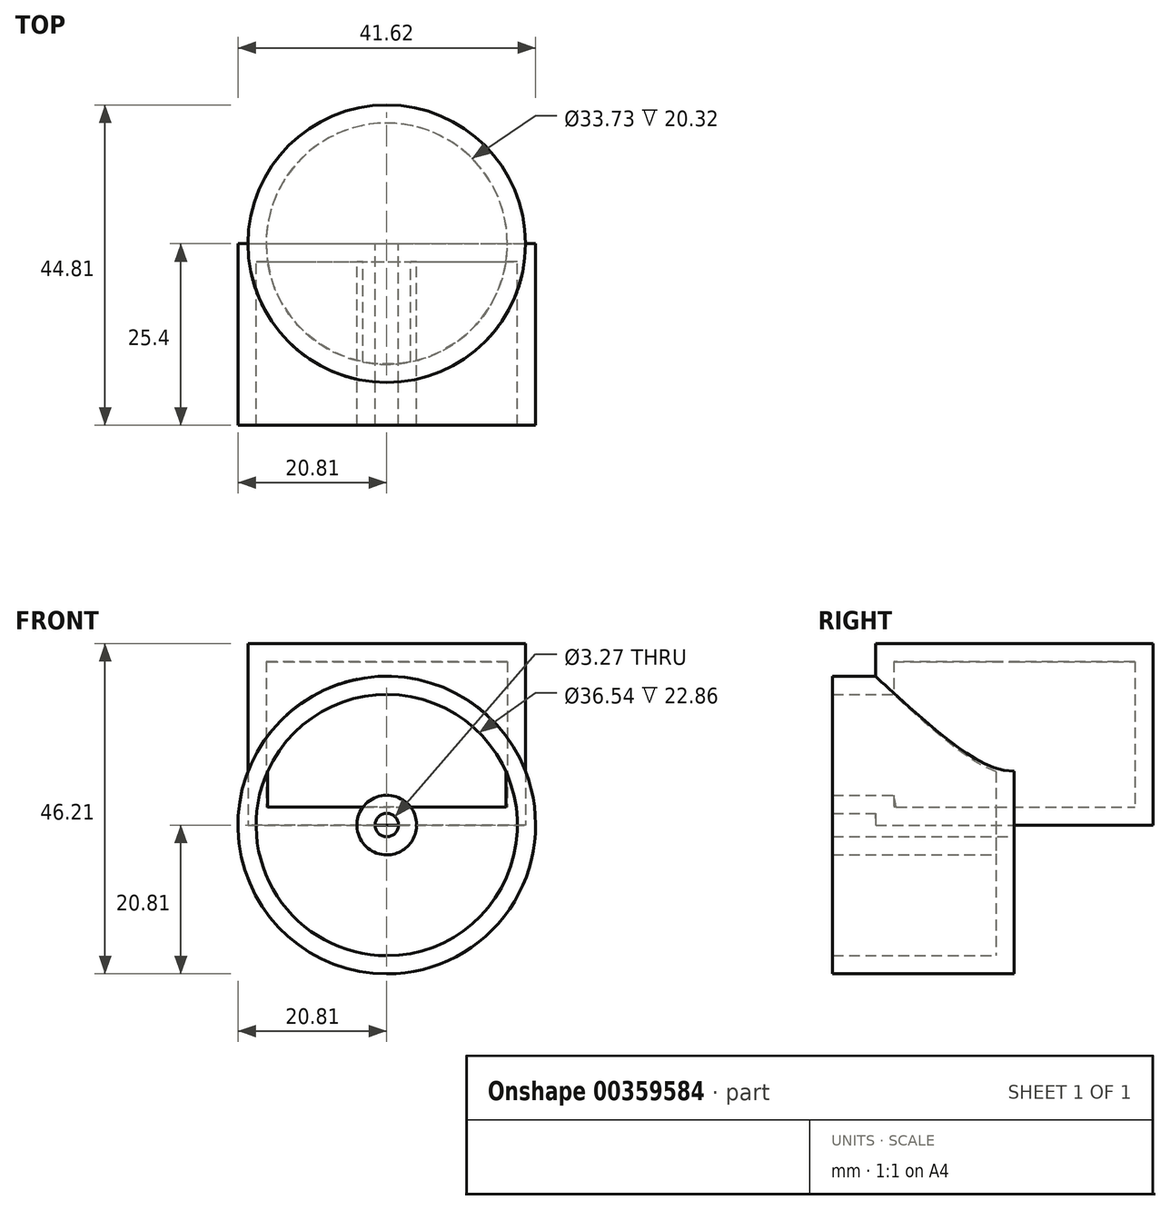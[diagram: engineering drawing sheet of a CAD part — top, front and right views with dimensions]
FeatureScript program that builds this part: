
annotation { "Feature Type Name" : "Feature", "Feature Type Description" : "" }
export const myFeature = defineFeature(function(context is Context, id is Id, definition is map)
    precondition{}
    {
        {
            var Q0;
            Q0=qCreatedBy(makeId("Top.planeOp"),FACE);
            var sketch = newSketch(context, id + "F0", { "sketchPlane" : qUnion([Q0])});
            skCircle(sketch, "E0", {"center": v(0, 0) * mm, "radius": 19.4 * mm});
            skSolve(sketch);
        }
        {
            var Q0;
            Q0=makeQuery(id+"F0.imprint","IMPRINT",FACE,{"disambiguationData":[TD([[makeQuery(id+"F0.imprint","IMPRINT",EDGE,{"derivedFrom":sQuery(id+"F0.wireOp",EDGE,"E0")}),1.0]])]});
            extrude(context, id + "F1", {"entities" : qUnion([Q0]), "depth" : 25.4 * mm});
        }
        {
            var Q0;
            Q0=qCreatedBy(makeId("Front.planeOp"),FACE);
            var sketch = newSketch(context, id + "F2", { "sketchPlane" : qUnion([Q0])});
            skCircle(sketch, "E1", {"center": v(0, 0) * mm, "radius": 1.63 * mm});
            skCircle(sketch, "E2", {"center": v(0, 0) * mm, "radius": 20.81 * mm});
            skSolve(sketch);
        }
        {
            var Q0;
            Q0=makeQuery(id+"F2.imprint","IMPRINT",FACE,{"disambiguationData":[TD([[makeQuery(id+"F2.imprint","IMPRINT",EDGE,{"derivedFrom":sQuery(id+"F2.wireOp",EDGE,"E1")}),-1.0]])]});
            extrude(context, id + "F3", {"entities" : qUnion([Q0]), "operationType" : NewBodyOperationType.ADD, "depth" : 25.4 * mm});
        }
        {
            var Q0;
            Q0=makeQuery(id+"F3.opExtrude","CAP_FACE",FACE,{"disambiguationData":[OSD([sQuery(id+"F2.wireOp",EDGE,"E1"),sQuery(id+"F2.wireOp",EDGE,"E2")])],"isStart":false});
            shell(context, id + "F4", {"entities" : qUnion([Q0]), "thickness" : 2.54 * mm});
        }
    });
